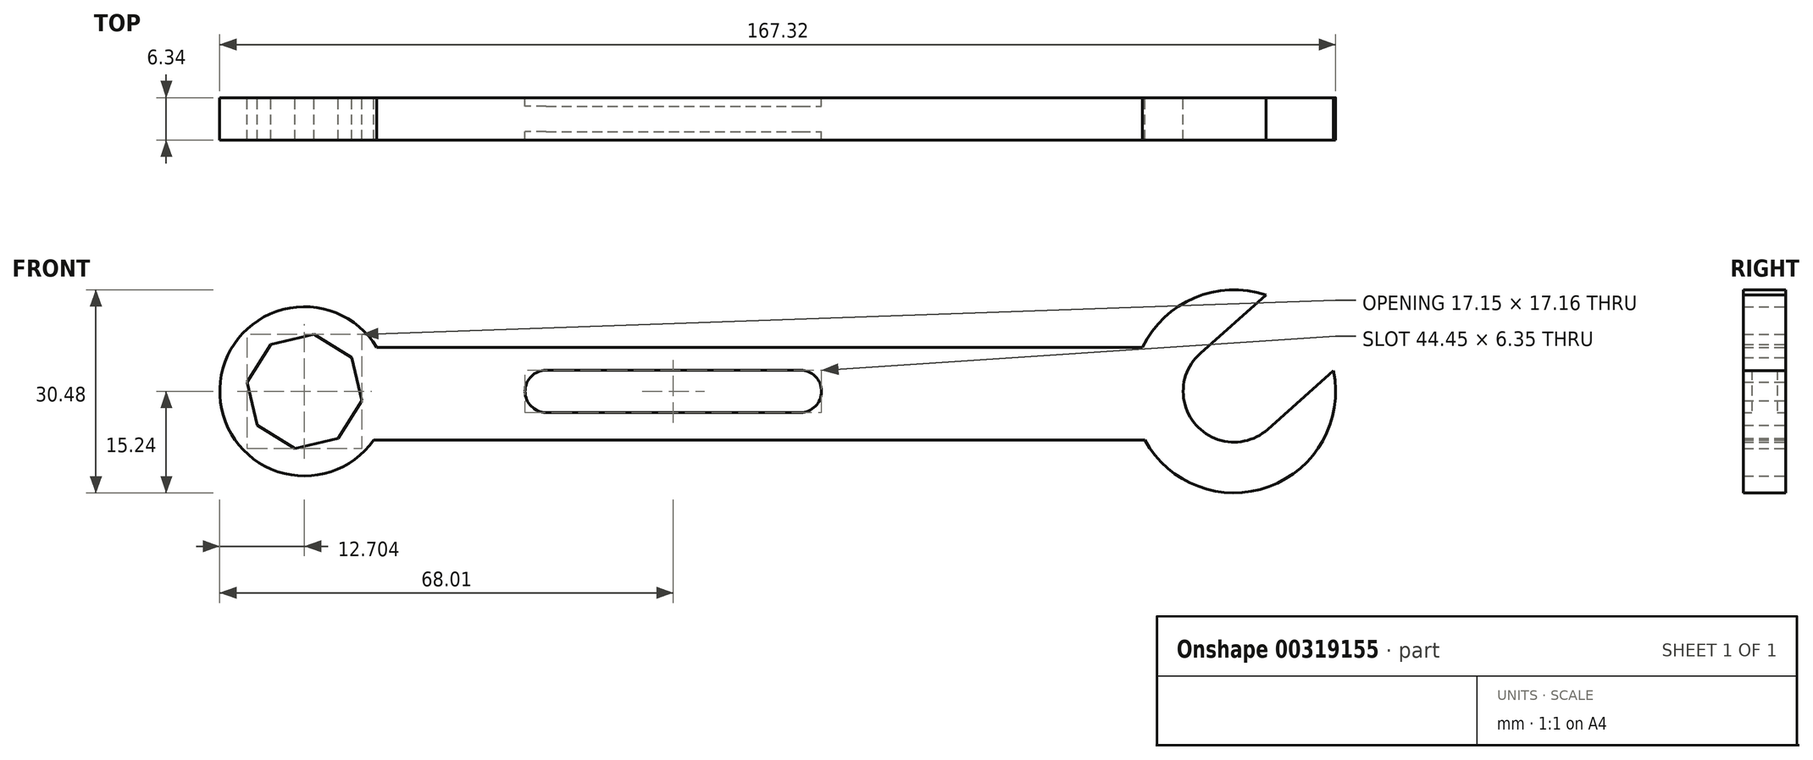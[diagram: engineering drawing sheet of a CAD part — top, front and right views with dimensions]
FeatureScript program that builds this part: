
annotation { "Feature Type Name" : "Feature", "Feature Type Description" : "" }
export const myFeature = defineFeature(function(context is Context, id is Id, definition is map)
    precondition{}
    {
        {
            var Q0;
            Q0=qCreatedBy(makeId("Front.planeOp"),FACE);
            var sketch = newSketch(context, id + "F0", { "sketchPlane" : qUnion([Q0])});
            skCircle(sketch, "E0", {"center": v(-55.3, 0) * mm, "radius": 12.7 * mm});
            skArc(sketch, "E1", {"start": v(88.87, 14.46) * mm, "mid": v(72.68, -10.12) * mm, "end": v(99, 3.07) * mm});
            skCircle(sketch, "E2.cCircle", {"center": v(-55.3, 0) * mm, "radius": 8.03 * mm, "construction": true});
            skLineSegment(sketch, "E2.0", {"start": v(-46.73, -1.41) * mm, "end": v(-50.24, -7.07) * mm});
            skLineSegment(sketch, "E2.1", {"start": v(-50.24, -7.07) * mm, "end": v(-56.72, -8.58) * mm});
            skLineSegment(sketch, "E2.2", {"start": v(-56.72, -8.58) * mm, "end": v(-62.37, -5.06) * mm});
            skLineSegment(sketch, "E2.3", {"start": v(-62.37, -5.06) * mm, "end": v(-63.88, 1.41) * mm});
            skLineSegment(sketch, "E2.4", {"start": v(-63.88, 1.41) * mm, "end": v(-60.37, 7.07) * mm});
            skLineSegment(sketch, "E2.5", {"start": v(-60.37, 7.07) * mm, "end": v(-53.9, 8.58) * mm});
            skLineSegment(sketch, "E2.6", {"start": v(-53.9, 8.58) * mm, "end": v(-48.24, 5.06) * mm});
            skLineSegment(sketch, "E2.7", {"start": v(-48.24, 5.06) * mm, "end": v(-46.73, -1.41) * mm});
            skPoint(sketch, "E2.0.midPoint", {"position": v(-48.49, -4.24) * mm});
            skLineSegment(sketch, "E3.1", {"start": v(94.82, -0.63) * mm, "end": v(89.13, -5.7) * mm});
            skLineSegment(sketch, "E3.3", {"start": v(79, 5.7) * mm, "end": v(84.7, 10.76) * mm});
            skPoint(sketch, "E3.0.midPoint", {"position": v(89.76, 5.06) * mm});
            skLineSegment(sketch, "E4", {"start": v(-44.46, 6.61) * mm, "end": v(70.34, 6.61) * mm});
            skLineSegment(sketch, "E5", {"start": v(-44.91, -7.3) * mm, "end": v(70.69, -7.3) * mm});
            skLineSegment(sketch, "E6", {"start": v(84.7, 10.76) * mm, "end": v(88.87, 14.46) * mm});
            skLineSegment(sketch, "E7", {"start": v(94.82, -0.63) * mm, "end": v(99, 3.07) * mm});
            skArc(sketch, "E8", {"start": v(-19.05, 3.18) * mm, "mid": v(-22.23, 0) * mm, "end": v(-19.05, -3.18) * mm});
            skArc(sketch, "E9", {"start": v(19.05, -3.18) * mm, "mid": v(22.23, 0) * mm, "end": v(19.05, 3.17) * mm});
            skLineSegment(sketch, "E10", {"start": v(-19.05, 3.18) * mm, "end": v(19.05, 3.17) * mm});
            skLineSegment(sketch, "E11", {"start": v(-19.05, -3.18) * mm, "end": v(19.05, -3.18) * mm});
            skPoint(sketch, "E12.orphan", {"position": v(73.3, 0.63) * mm});
            skArc(sketch, "E13", {"start": v(79, 5.7) * mm, "mid": v(78.37, -5.06) * mm, "end": v(89.13, -5.7) * mm});
            skSolve(sketch);
        }
        {
            var Q0;
            Q0=makeQuery(id+"F0.imprint","IMPRINT",FACE,{"disambiguationData":[TD([[makeQuery(id+"F0.imprint","IMPRINT",EDGE,{"derivedFrom":sQuery(id+"F0.wireOp",EDGE,"E2.0")}),1.0]])]});
            var Q1;
            {var subQ0=sQuery(id+"F0.wireOp",EDGE,"E4");Q1=makeQuery(id+"F0.imprint","IMPRINT",FACE,{"disambiguationData":[TD([[makeQuery(id+"F0.imprint","IMPRINT",EDGE,{"derivedFrom":subQ0}),-1.0]])]});}
            var Q2;
            Q2=makeQuery(id+"F0.imprint","IMPRINT",FACE,{"disambiguationData":[TD([[makeQuery(id+"F0.imprint","IMPRINT",EDGE,{"derivedFrom":sQuery(id+"F0.wireOp",EDGE,"E3.1")}),1.0]])]});
            extrude(context, id + "F1", {"entities" : qUnion([Q0, Q1, Q2]), "endBound" : BoundingType.SYMMETRIC, "depth" : 6.35 * mm});
        }
        {
            var Q0;
            Q0=makeQuery(id+"F0.imprint","IMPRINT",FACE,{"disambiguationData":[TD([[makeQuery(id+"F0.imprint","IMPRINT",EDGE,{"derivedFrom":sQuery(id+"F0.wireOp",EDGE,"E8")}),1.0]])]});
            extrude(context, id + "F2", {"entities" : qUnion([Q0]), "operationType" : NewBodyOperationType.ADD, "endBound" : BoundingType.SYMMETRIC, "depth" : 3.8 * mm});
        }
    });
